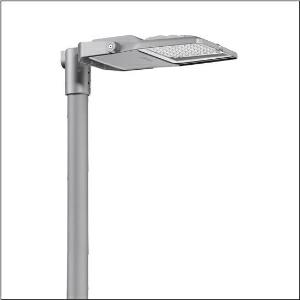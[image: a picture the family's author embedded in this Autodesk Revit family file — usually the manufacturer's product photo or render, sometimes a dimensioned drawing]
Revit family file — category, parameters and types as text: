
# Revit family: floodlight_fl_21_iq_mini___pl43_5xa7771b2a3a_6d21
name_source: partatom
category: Lighting Fixtures
units: mm (PartAtom-declared; Revit-internal decimal feet)

## family parameters
Cut with Voids When Loaded = No
Host = Face
Light Source = No
Part Type = Normal
Room Calculation Point = No
Round Connector Dimension = Use Diameter
Shared = No

## types (1)
- --- (1 x LED, 6400 lm, 45.5 W, 3000K)
    Apparent Load = 46 VA
    CIE Flux Codes = 27 78 99 100 100
    Color Rendering = 70
    Color Temperature = 3000K
    Default Elevation = 1800 mm
    Description = Floodlight FL 21 iQ mini, floodlight, primary light control with lens, of PMMA, primary optical cover: protective disc, of toughened safety glass, transparent, light distribution: PL43, light emission: direct distribution, installation type: surface-mounted, LED, High Power LED, rated luminous flux: 6.400lm, luminous efficacy: 141lm/W, light colour: 730, colour temperature: 3000K, control: Auto-Match, Temp-Guard, Lumen-Switch, Night-Set, Smart-Wire, Light-Fading, Desk-Remote (wireless, voltage-free reading and setting of iQ features in the workshop via application-optimized NFC function/RFID function), optimised constant luminous flux control (CLO 2.0), with terminal, 6-pole, mains connection: 220..240V, AC, 50/60Hz, start of lifetime: 46W, end of service life: 48W, reduction: 22W, luminaire housing, of diecast aluminium, powder-coated, Siteco® metallic grey (DB 702S), corrosivity category C5 mid according to DIN EN ISO 12944, sealing non-destructively replaceable, please order mast flange separately, mast bracket, of steel, galvanised, powder-coated, Siteco® metallic grey (DB 702S), protection rating (complete): IP66, insulation class (complete): insulation class II (safety insulation), certification: CE, ENEC, VDE, protection symbol: D, impact resistance: IK08, permissible operating ambient temperature: -40..+40°C, permissible operating ambient temperature for outdoor applications: -40..+50°C, standard: DIN EN 12944, LABS conformity tested according to VDMA 24364:2018-05, packaging unit: 1 piece

Light Distribution: PL43
    Height = 70 mm
    Lamp = 1 x LED
    Lamp Light Flux = 6400 lm
    Lamp Power = 45.5 W
    Lamp count = 1
    Length = 485 mm
    Luminous efficacy = 141 lm/W
    Manufacturer = Siteco
    ModVariant = No
    Model = 5XA7771B2A3A
    Number of Poles = 1
    OnlyDefault = Yes
    Power Factor = 1
    Product Name = Floodlight FL 21 iQ mini | PL43
    Product group = floodlight | pylon annexe
    ProductGroupID = 6200
    Protection Class = Protection class II
    Protection Degree = IP 66
    RLX_Detail_Level = 1
    RLX_Emergency_Light_Flux = 0 lm
    RLX_Emergency_Type = 0
    RLX_Emergency_Type_DB = No
    RlxData = <blob elided: 101121 chars, md5=8ec4903e>
    Socket = socket
    Standby Power = 0 W
    System Light Flux = 6400 lm
    System Power = 46 W
    Type Comments = factory setting: luminous flux: 100 % | dim-lin: 254 | 463 mA
    Type Image = l_1007125.jpg
    URL = http://relux.com
    VarID = @adj_113157
    Voltage = 0 V
    Weight = 0.00 kg
    Width = 337 mm

## geometry (parser evidence)
native form markers: Blend x4, Sweep x13
no freeform markers — native parametric forms only
